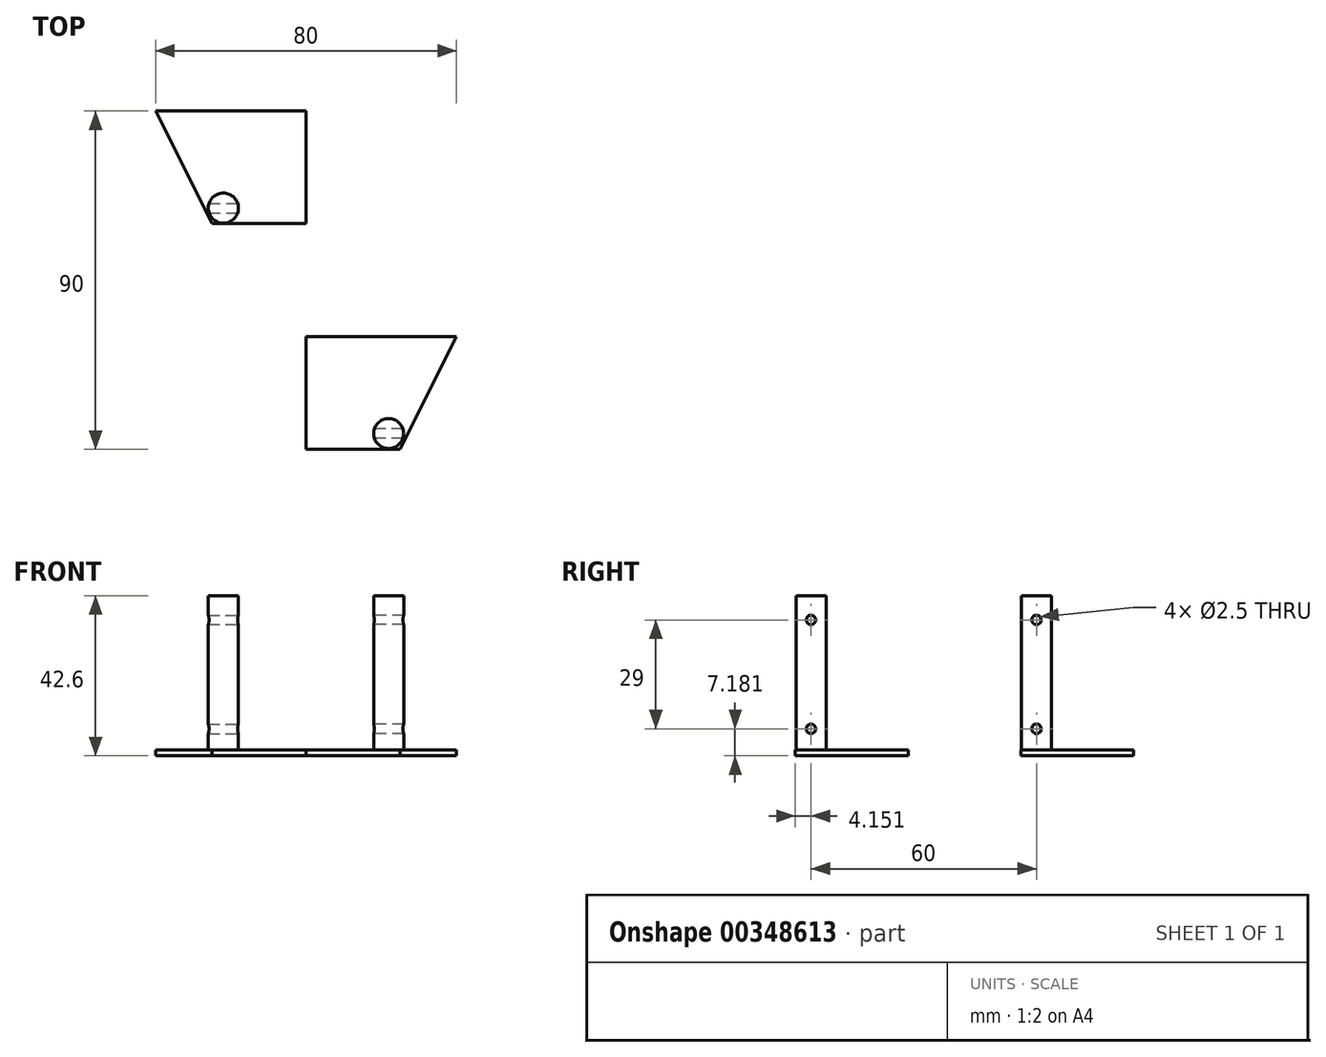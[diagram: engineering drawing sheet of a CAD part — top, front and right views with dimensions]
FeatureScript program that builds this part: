
annotation { "Feature Type Name" : "Feature", "Feature Type Description" : "" }
export const myFeature = defineFeature(function(context is Context, id is Id, definition is map)
    precondition{}
    {
        {
            var Q0;
            Q0=qCreatedBy(makeId("Top.planeOp"),FACE);
            var sketch = newSketch(context, id + "F0", { "sketchPlane" : qUnion([Q0])});
            skLineSegment(sketch, "E0", {"start": v(-24.55, -22.95) * mm, "end": v(0.45, -22.95) * mm});
            skLineSegment(sketch, "E1", {"start": v(0.45, -22.95) * mm, "end": v(15.45, 7.05) * mm});
            skLineSegment(sketch, "E2", {"start": v(15.45, 7.05) * mm, "end": v(-24.55, 7.05) * mm});
            skLineSegment(sketch, "E3", {"start": v(-24.55, 7.05) * mm, "end": v(-24.55, -22.95) * mm});
            skCircle(sketch, "E4", {"center": v(-2.56, -18.8) * mm, "radius": 4 * mm});
            skSolve(sketch);
        }
        {
            var Q0;
            Q0 = qSketchRegion(id + "F0", true);
            extrude(context, id + "F1", {"entities" : qUnion([Q0]), "depth" : 1.6 * mm});
        }
        {
            var Q0;
            Q0=makeQuery(id+"F0.imprint","IMPRINT",FACE,{"disambiguationData":[TD([[makeQuery(id+"F0.imprint","IMPRINT",EDGE,{"derivedFrom":sQuery(id+"F0.wireOp",EDGE,"E4")}),1.0]])]});
            extrude(context, id + "F2", {"entities" : qUnion([Q0]), "operationType" : NewBodyOperationType.ADD, "depth" : 42.6 * mm});
        }
        {
            var Q0;
            Q0=qCreatedBy(makeId("Right.planeOp"),FACE);
            var sketch = newSketch(context, id + "F3", { "sketchPlane" : qUnion([Q0])});
            skCircle(sketch, "E5", {"center": v(-18.8, 7.18) * mm, "radius": 1.25 * mm});
            skCircle(sketch, "E6", {"center": v(-18.8, 36.18) * mm, "radius": 1.25 * mm});
            skLineSegment(sketch, "E7.bottom", {"start": v(-22.8, 41.58) * mm, "end": v(-14.8, 41.58) * mm});
            skLineSegment(sketch, "E7.top", {"start": v(-22.8, 1.58) * mm, "end": v(-14.8, 1.58) * mm});
            skLineSegment(sketch, "E7.left", {"start": v(-22.8, 41.58) * mm, "end": v(-22.8, 1.58) * mm});
            skLineSegment(sketch, "E7.right", {"start": v(-14.8, 41.58) * mm, "end": v(-14.8, 1.58) * mm});
            skSolve(sketch);
        }
        {
            var Q0;
            Q0=makeQuery(id+"F3.imprint","IMPRINT",FACE,{"disambiguationData":[TD([[makeQuery(id+"F3.imprint","IMPRINT",EDGE,{"derivedFrom":sQuery(id+"F3.wireOp",EDGE,"E6")}),1.0]])]});
            var Q1;
            Q1=makeQuery(id+"F3.imprint","IMPRINT",FACE,{"disambiguationData":[TD([[makeQuery(id+"F3.imprint","IMPRINT",EDGE,{"derivedFrom":sQuery(id+"F3.wireOp",EDGE,"E5")}),1.0]])]});
            extrude(context, id + "F4", {"entities" : qUnion([Q0, Q1]), "operationType" : NewBodyOperationType.REMOVE, "endBound" : BoundingType.SYMMETRIC, "depth" : 25 * mm});
        }
        {
            var Q0;
            Q0=makeQuery(id+"F1.opExtrude","SWEPT_BODY",BODY,{"disambiguationData":[OSD([sQuery(id+"F0.wireOp",EDGE,"E0"),sQuery(id+"F0.wireOp",EDGE,"E1"),sQuery(id+"F0.wireOp",EDGE,"E2"),sQuery(id+"F0.wireOp",EDGE,"E3"),sQuery(id+"F0.wireOp",EDGE,"E4")])]});
            var Q1;
            Q1=qCreatedBy(makeId("Top.planeOp"),FACE);
            mirror(context, id + "F5", {"entities" : qUnion([Q0]), "mirrorPlane" : qUnion([Q1])});
        }
        {
            var Q0;
            Q0=makeQuery(id+"F5.opPattern","COPY",BODY,{"derivedFrom":makeQuery(id+"F1.opExtrude","SWEPT_BODY",BODY,{"disambiguationData":[OSD([sQuery(id+"F0.wireOp",EDGE,"E0"),sQuery(id+"F0.wireOp",EDGE,"E1"),sQuery(id+"F0.wireOp",EDGE,"E2"),sQuery(id+"F0.wireOp",EDGE,"E3"),sQuery(id+"F0.wireOp",EDGE,"E4")])]}),"instanceName":"1"});
            transform(context, id + "F6", {"entities" : qUnion([Q0]), "transformType" : TransformType.TRANSLATION_3D, "dx" : 0 * mm, "dy" : 60 * mm, "dz" : 0 * mm, "makeCopy" : true});
        }
        {
            var Q0;
            Q0=makeQuery(id+"F5.opPattern","COPY",BODY,{"derivedFrom":makeQuery(id+"F1.opExtrude","SWEPT_BODY",BODY,{"disambiguationData":[OSD([sQuery(id+"F0.wireOp",EDGE,"E0"),sQuery(id+"F0.wireOp",EDGE,"E1"),sQuery(id+"F0.wireOp",EDGE,"E2"),sQuery(id+"F0.wireOp",EDGE,"E3"),sQuery(id+"F0.wireOp",EDGE,"E4")])]}),"instanceName":"1"});
            deleteBodies(context, id + "F7", {"entities" : qUnion([Q0])});
        }
        {
            var Q0;
            Q0=makeQuery(id+"F6.opPattern","COPY",BODY,{"derivedFrom":makeQuery(id+"F5.opPattern","COPY",BODY,{"derivedFrom":makeQuery(id+"F1.opExtrude","SWEPT_BODY",BODY,{"disambiguationData":[OSD([sQuery(id+"F0.wireOp",EDGE,"E0"),sQuery(id+"F0.wireOp",EDGE,"E1"),sQuery(id+"F0.wireOp",EDGE,"E2"),sQuery(id+"F0.wireOp",EDGE,"E3"),sQuery(id+"F0.wireOp",EDGE,"E4")])]}),"instanceName":"1"}),"instanceName":"1"});
            var Q1;
            Q1=makeQuery(id+"F6.opPattern","COPY",EDGE,{"derivedFrom":makeQuery(id+"F5.opPattern","COPY",EDGE,{"derivedFrom":makeQuery(id+"F1.opExtrude","CAP_EDGE",EDGE,{"disambiguationData":[OSD([sQuery(id+"F0.wireOp",EDGE,"E3")])],"isStart":true}),"instanceName":"1"}),"instanceName":"1"});
            transform(context, id + "F8", {"entities" : qUnion([Q0]), "transformType" : TransformType.ROTATION, "transformAxis" : qUnion([Q1]), "angle" : 180 * degree, "makeCopy" : false});
        }
    });
